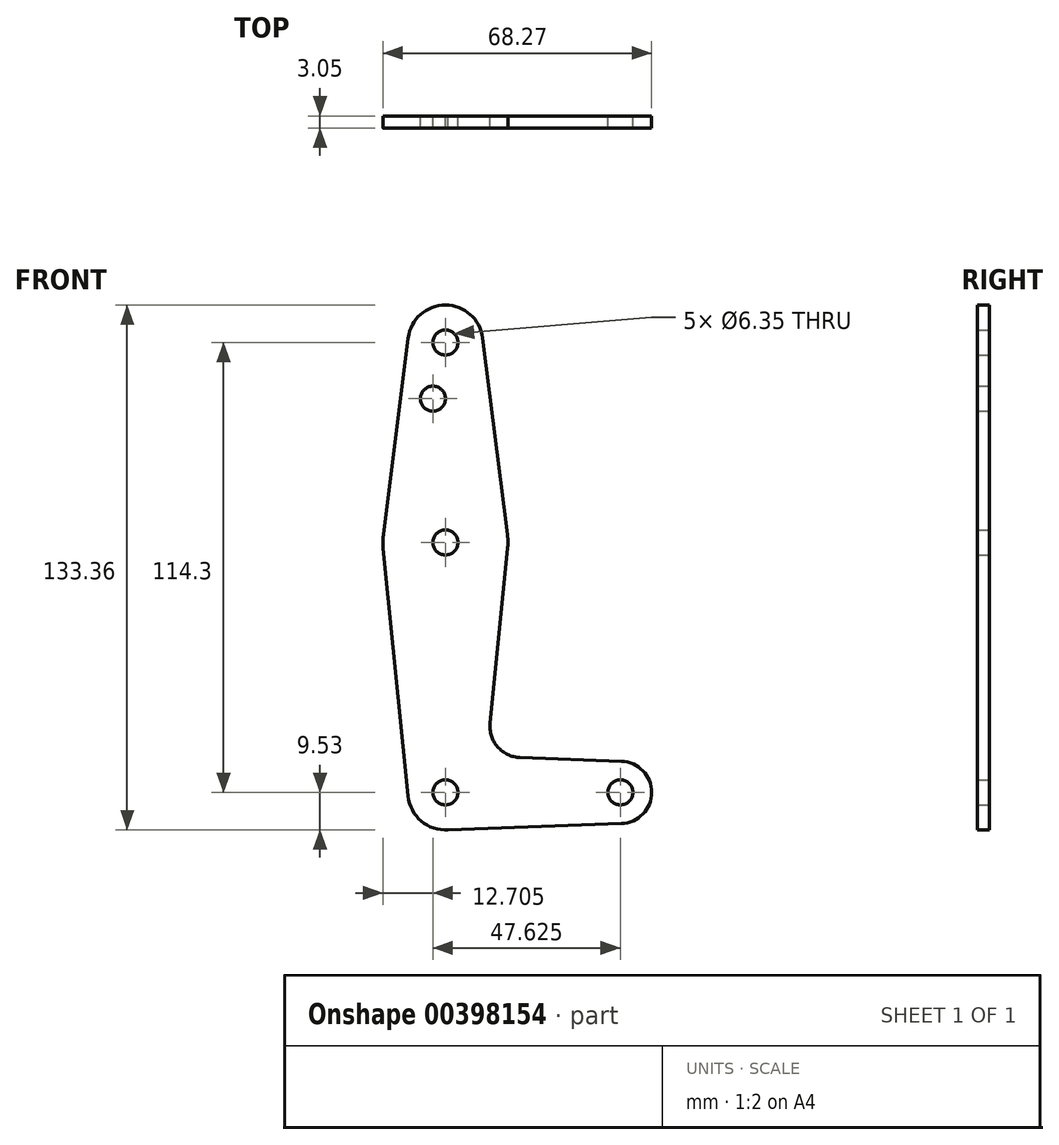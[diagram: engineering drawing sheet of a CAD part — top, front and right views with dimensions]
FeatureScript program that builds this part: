
annotation { "Feature Type Name" : "Feature", "Feature Type Description" : "" }
export const myFeature = defineFeature(function(context is Context, id is Id, definition is map)
    precondition{}
    {
        {
            var Q0;
            Q0=qCreatedBy(makeId("Front.planeOp"),FACE);
            var sketch = newSketch(context, id + "F0", { "sketchPlane" : qUnion([Q0])});
            skLineSegment(sketch, "E0", {"start": v(0, 114.3) * mm, "end": v(0, 0) * mm, "construction": true});
            skLineSegment(sketch, "E1", {"start": v(0, 0) * mm, "end": v(44.45, 0) * mm, "construction": true});
            skCircle(sketch, "E2", {"center": v(0, 114.3) * mm, "radius": 9.53 * mm});
            skCircle(sketch, "E3", {"center": v(0, 63.5) * mm, "radius": 15.88 * mm});
            skCircle(sketch, "E4", {"center": v(0, 0) * mm, "radius": 9.53 * mm});
            skCircle(sketch, "E5", {"center": v(44.45, 0) * mm, "radius": 7.94 * mm});
            skLineSegment(sketch, "E6", {"start": v(18.97, 8.85) * mm, "end": v(44.73, 7.93) * mm});
            skLineSegment(sketch, "E7", {"start": v(0, -9.53) * mm, "end": v(44.73, -7.93) * mm});
            skLineSegment(sketch, "E8", {"start": v(9.45, 115.5) * mm, "end": v(15.75, 65.48) * mm});
            skLineSegment(sketch, "E9", {"start": v(-9.45, 115.5) * mm, "end": v(-15.75, 65.48) * mm});
            skLineSegment(sketch, "E10", {"start": v(11.34, 17.6) * mm, "end": v(15.8, 61.91) * mm});
            skLineSegment(sketch, "E11", {"start": v(-15.8, 61.91) * mm, "end": v(-9.48, -0.95) * mm});
            skCircle(sketch, "E12", {"center": v(0, 114.3) * mm, "radius": 3.18 * mm});
            skCircle(sketch, "E13", {"center": v(0, 0) * mm, "radius": 3.18 * mm});
            skCircle(sketch, "E14", {"center": v(44.45, 0) * mm, "radius": 3.18 * mm});
            skCircle(sketch, "E15", {"center": v(0, 63.5) * mm, "radius": 3.18 * mm});
            skArc(sketch, "E16.filletArc", {"start": v(11.34, 17.6) * mm, "mid": v(13.26, 11.57) * mm, "end": v(18.97, 8.85) * mm});
            skCircle(sketch, "E17", {"center": v(-3.17, 100.03) * mm, "radius": 3.18 * mm});
            skSolve(sketch);
        }
        {
            var Q0;
            Q0 = qSketchRegion(id + "F0", true);
            extrude(context, id + "F1", {"entities" : qUnion([Q0]), "depth" : 3.05 * mm});
        }
    });
